# Revit family: JASMIN plafoniera
name_source: partatom
category: Lighting Fixtures
revit_build: Autodesk Revit Architecture 2015 (Build: 20140322_1515(x64)
units: mm (PartAtom-declared; Revit-internal decimal feet)

## types (9) — shared parameters
Color Filter = 16777215
Dimming Lamp Color Temperature Shift = <None>
Emit Shape Visible in Rendering = Yes
IP = IP20
Klasyfikacja obciążenia = Oświetlenie
Manufacturer = KANLUX
Materiał klosz = KANLUX - klosz - szkło satynowe
Photometric Web File = generic
Tilt Angle = 90.00°
URL = www.kanlux.pl
Współczynnik mocy = 1
Wysokość = 77 mm
zero-valued in all types: Default Elevation

## per-type parameters (varying)
| type | Apparent Load | Emit from Circle Diameter | Kod | Materiał obudowa | Moc oprawy | Model | Wattage Comments | Średnica | Średnica klosza |
| KANLUX JASMIN plafoniera 370-W 23124 biały dąb | 120 VA | 335 mm | 23124 | KANLUX - obudowa - biały dąb | 120 W | JASMIN 370-W | 120 | 375 mm | 335 mm |
| KANLUX JASMIN plafoniera 270-W 23123 biały dąb | 60 VA | 235 mm  [stored 0.770997 ft] | 23123 | KANLUX - obudowa - biały dąb | 60 W | JASMIN 270-W | 60 | 275 mm | 235 mm  [stored 0.770997 ft] |
| KANLUX JASMIN plafoniera 470-W 23125 biały dąb | 120 VA | 435 mm | 23125 | KANLUX - obudowa - biały dąb | 120 W | JASMIN 470-W | 120 | 475 mm | 435 mm |
| KANLUX JASMIN plafoniera 270-WE 23120 wenge | 60 VA | 235 mm  [stored 0.770997 ft] | 23120 | KANLUX - obudowa - wenge | 60 W | JASMIN 270-WE | 60 | 275 mm | 235 mm  [stored 0.770997 ft] |
| KANLUX JASMIN plafoniera 370-WE 23121 wenge | 120 VA | 335 mm | 23121 | KANLUX - obudowa - wenge | 120 W | JASMIN 370-WE | 120 | 375 mm | 335 mm |
| KANLUX JASMIN plafoniera 470-WE 23122 wenge | 120 VA | 435 mm | 23122 | KANLUX - obudowa - wenge | 120 W | JASMIN 470-WE | 120 | 475 mm | 435 mm |
| KANLUX JASMIN plafoniera 270-W/M 23126 biały matowy | 60 VA | 235 mm  [stored 0.770997 ft] | 23126 | KANLUX - obudowa - biały matowy | 60 W | JASMIN 270-W/M | 60 | 275 mm | 235 mm  [stored 0.770997 ft] |
| KANLUX JASMIN plafoniera 370-W/M 23127 biały matowy | 120 VA | 335 mm | 23127 | KANLUX - obudowa - biały matowy | 120 W | JASMIN 370-W/M | 120 | 375 mm | 335 mm |
| KANLUX JASMIN plafoniera 470-W/M 23128 biały matowy | 120 VA | 435 mm | 23128 | KANLUX - obudowa - biały matowy | 120 W | JASMIN 470-W/M | 120 | 475 mm | 435 mm |

note: [stored X ft] marks values corroborated as IEEE doubles in the binary element streams (Revit-internal decimal feet)
